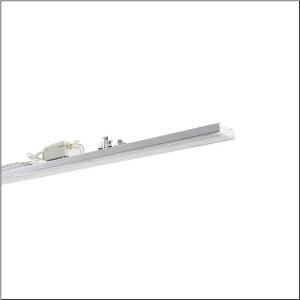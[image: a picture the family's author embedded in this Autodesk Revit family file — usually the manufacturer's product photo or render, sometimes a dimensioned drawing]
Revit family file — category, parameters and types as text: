
# Revit family: licross_r__21_recessed_ho_52tl12dv4l2m3c_e532
name_source: partatom
category: Lighting Fixtures
units: mm (PartAtom-declared; Revit-internal decimal feet)

## family parameters
Cut with Voids When Loaded = No
Host = Face
Light Source = No
Part Type = Normal
Room Calculation Point = No
Round Connector Dimension = Use Diameter
Shared = No

## types (1)
- --- (1 x LED, 910 lm, 6.4 W, 4000K)
    Apparent Load = 6 VA
    CIE Flux Codes = 69 91 98 100 100
    Color Rendering = 80
    Color Temperature = 4000K
    Default Elevation = 1800 mm
    Description = Licross® 21 Recessed HO, luminaire insert, of sheet steel, galvanised, coil coated, white, length: 2.250mm, width: 66mm, height: 67mm, LED rated luminous flux: 22.710lm, light colour: 840, control gear: DALI 2, with plug, 6-pole, with phase selection, for trunking rail, 14-core, mains connection: 220..240V, AC, 50/60Hz, rated input power: 129W, for trunking rail, 14-core, halogen-free wiring, for emergency light function, converter,control gear: single battery element, battery: LiFeP04, 9Ah, primary optical cover: cover, of PMMA, light emission: direct distribution, primary light characteristic: symmetric, protection rating (complete): IP40, insulation class (complete): insulation class I (protective earthing), certification: CE, UKCA, protection symbol: D if used in an environment without relevant dust loads with corresponding accessories, impact resistance: IK06, permissible ambient temperature for indoor applications: +5..+30°C, standard: EN 60598-2-22, LABS conformity tested according to VDMA 24364:2018-05, reducing of maximum allowable ambient temperature of 5°C with ceiling mounting, corresponds to IFS (International Featured Standards) requirements for safety and quality in the food industry, packaging unit: 1 piece
    Height = 58 mm
    Lamp = 1 x LED
    Lamp Light Flux = 910 lm
    Lamp Power = 6.4 W
    Lamp count = 1
    Length = 2250 mm
    Luminous efficacy = 142 lm/W
    Manufacturer = Siteco
    ModVariant = No
    Model = 52TL12DV4L2M3C
    Mounting Place = Ceiling
    Mounting Type = Pendant
    Number of Poles = 1
    OnlyDefault = Yes
    Power Factor = 1
    Product Name = Licross® 21 Recessed HO
    Product group = luminaire insert
    ProductGroupID = 901
    Protection Class = Protection class I
    Protection Degree = IP 40
    RLX_Detail_Level = 1
    RLX_Emergency_Light_Flux = 0 lm
    RLX_Emergency_Type = 0
    RLX_Emergency_Type_DB = No
    RlxData = <blob elided: 30221 chars, md5=ae14b453>
    Socket = socket
    Standby Power = 0 W
    System Light Flux = 910 lm
    System Power = 6 W
    Type Comments = : emergency light operation: 3 h
    Type Image = l_1296930.jpg
    URL = http://relux.com
    VarID = @adj_039459
    Voltage = 0 V
    Weight = 0.00 kg
    Width = 66 mm

## geometry (parser evidence)
native form markers: Blend x4, Sweep x9
no freeform markers — native parametric forms only
